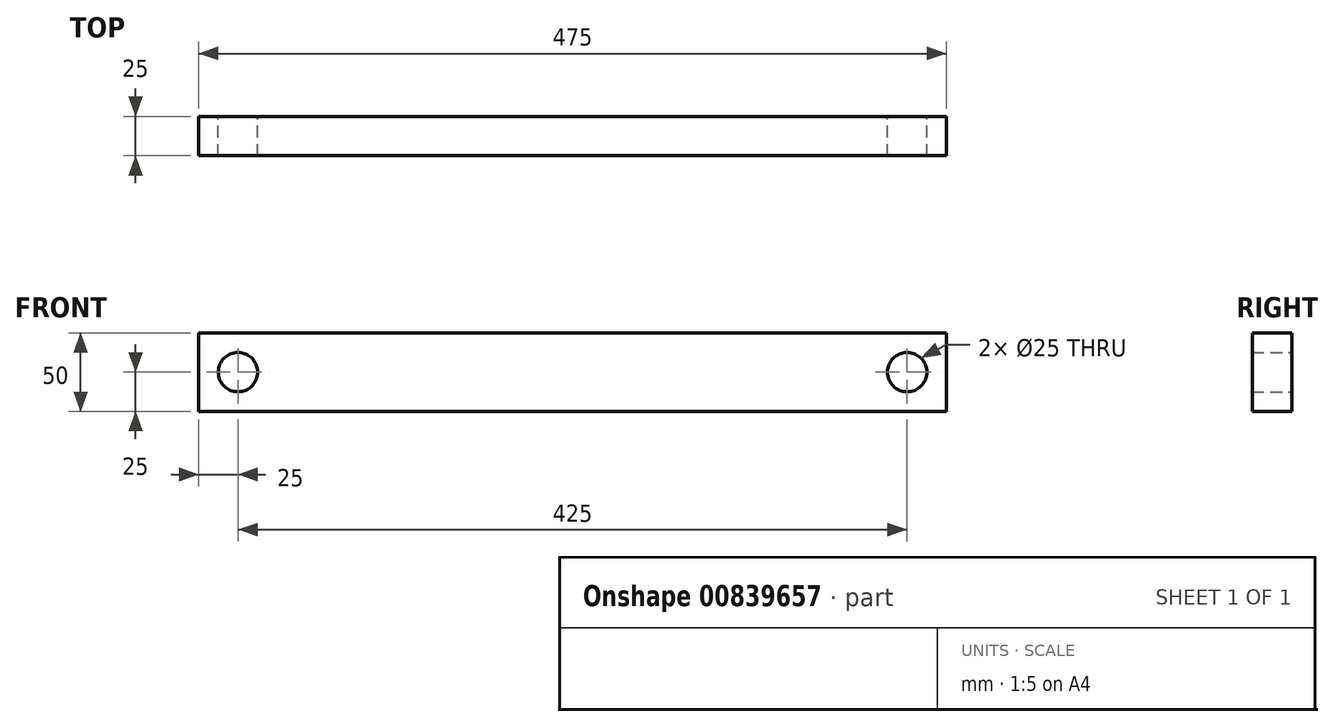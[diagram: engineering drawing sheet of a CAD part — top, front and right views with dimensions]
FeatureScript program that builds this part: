
annotation { "Feature Type Name" : "Feature", "Feature Type Description" : "" }
export const myFeature = defineFeature(function(context is Context, id is Id, definition is map)
    precondition{}
    {
        {
            var Q0;
            Q0=qCreatedBy(makeId("Front.planeOp"),FACE);
            var sketch = newSketch(context, id + "F0", { "sketchPlane" : qUnion([Q0])});
            skLineSegment(sketch, "E0.bottom", {"start": v(0, 0) * mm, "end": v(-475, 0) * mm});
            skLineSegment(sketch, "E0.top", {"start": v(0, -50) * mm, "end": v(-475, -50) * mm});
            skLineSegment(sketch, "E0.left", {"start": v(0, 0) * mm, "end": v(0, -50) * mm});
            skLineSegment(sketch, "E0.right", {"start": v(-475, 0) * mm, "end": v(-475, -50) * mm});
            skLineSegment(sketch, "E1", {"start": v(0, 0) * mm, "end": v(-50, -50) * mm});
            skCircle(sketch, "E2", {"center": v(-25, -25) * mm, "radius": 12.5 * mm});
            skLineSegment(sketch, "E3", {"start": v(-475, 0) * mm, "end": v(-425, -50) * mm});
            skCircle(sketch, "E4", {"center": v(-450, -25) * mm, "radius": 12.5 * mm});
            skSolve(sketch);
        }
        {
            var Q0;
            Q0=makeQuery(id+"F0.imprint","IMPRINT",FACE,{"disambiguationData":[TD([[makeQuery(id+"F0.imprint","IMPRINT",EDGE,{"derivedFrom":sQuery(id+"F0.wireOp",EDGE,"E0.bottom")}),1.0]])]});
            var Q1;
            {var subQ5=sQuery(id+"F0.wireOp",EDGE,"E0.left");Q1=makeQuery(id+"F0.imprint","IMPRINT",FACE,{"disambiguationData":[TD([[makeQuery(id+"F0.imprint","IMPRINT",EDGE,{"derivedFrom":subQ5}),-1.0]])]});}
            var Q2;
            {var subQ1=sQuery(id+"F0.wireOp",EDGE,"E0.right");Q2=makeQuery(id+"F0.imprint","IMPRINT",FACE,{"disambiguationData":[TD([[makeQuery(id+"F0.imprint","IMPRINT",EDGE,{"derivedFrom":subQ1}),1.0]])]});}
            extrude(context, id + "F1", {"entities" : qUnion([Q0, Q1, Q2]), "depth" : 25 * mm, "offsetDistance" : 25 * mm});
        }
    });
